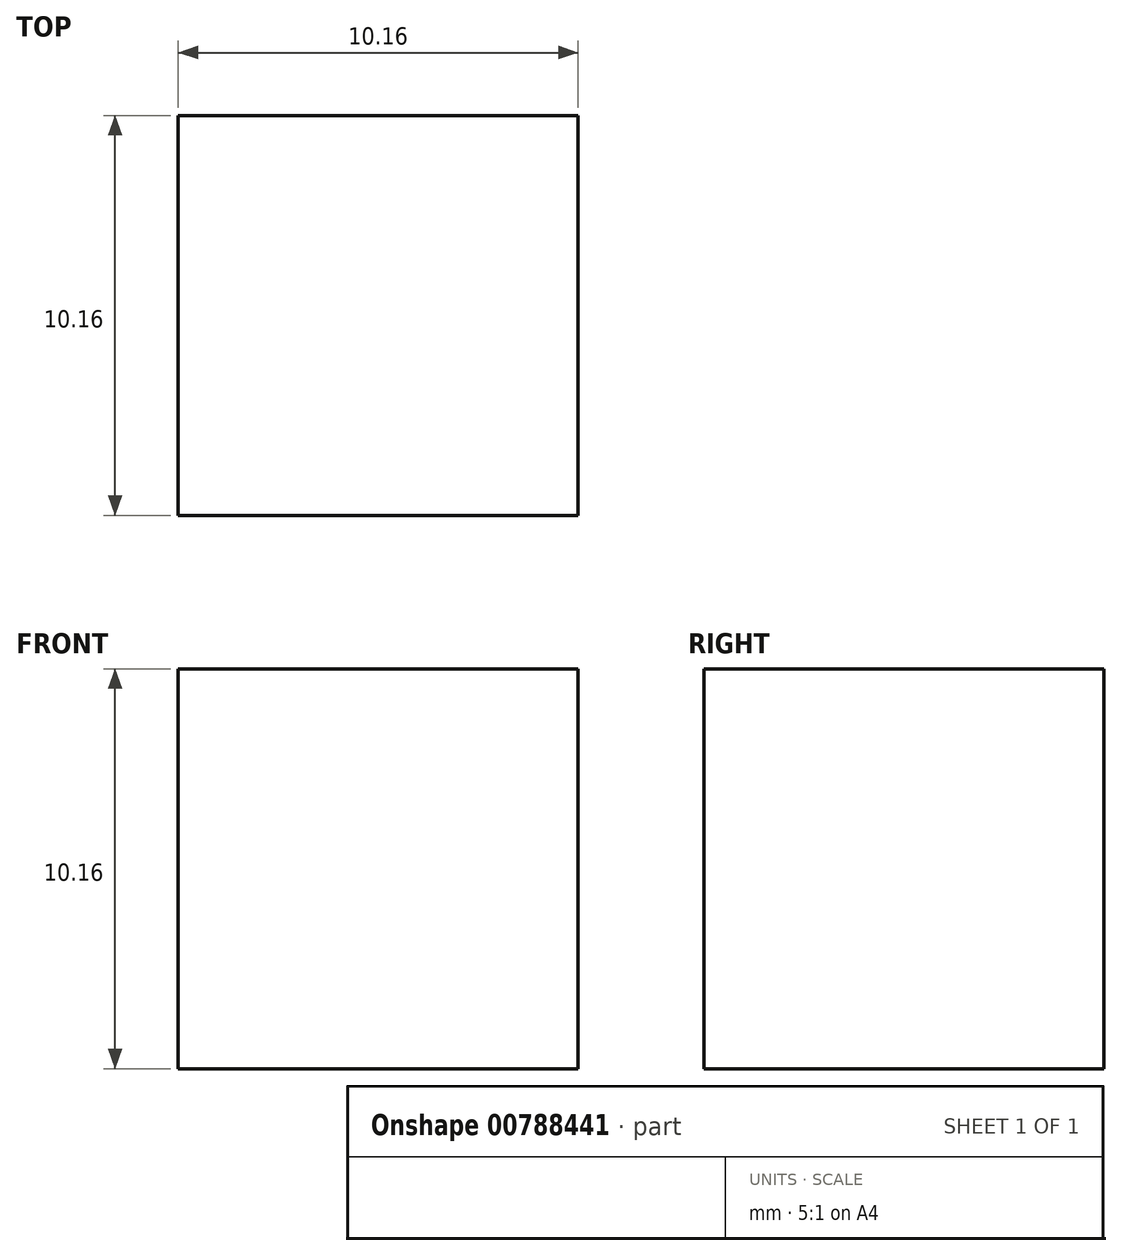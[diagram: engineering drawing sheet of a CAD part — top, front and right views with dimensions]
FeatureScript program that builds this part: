
annotation { "Feature Type Name" : "Feature", "Feature Type Description" : "" }
export const myFeature = defineFeature(function(context is Context, id is Id, definition is map)
    precondition{}
    {
        {
            var Q0;
            Q0=qCreatedBy(makeId("Top.planeOp"),FACE);
            var sketch = newSketch(context, id + "F0", { "sketchPlane" : qUnion([Q0])});
            skLineSegment(sketch, "E0.bottom", {"start": v(-12.3, 5.5) * mm, "end": v(-2.15, 5.5) * mm});
            skLineSegment(sketch, "E0.top", {"start": v(-12.3, -4.65) * mm, "end": v(-2.15, -4.65) * mm});
            skLineSegment(sketch, "E0.left", {"start": v(-12.3, 5.5) * mm, "end": v(-12.3, -4.65) * mm});
            skLineSegment(sketch, "E0.right", {"start": v(-2.15, 5.5) * mm, "end": v(-2.15, -4.65) * mm});
            skSolve(sketch);
        }
        {
            var Q0;
            Q0 = qSketchRegion(id + "F0", true);
            extrude(context, id + "F1", {"entities" : qUnion([Q0]), "depth" : 10.16 * mm, "offsetDistance" : 25.4 * mm});
        }
    });
